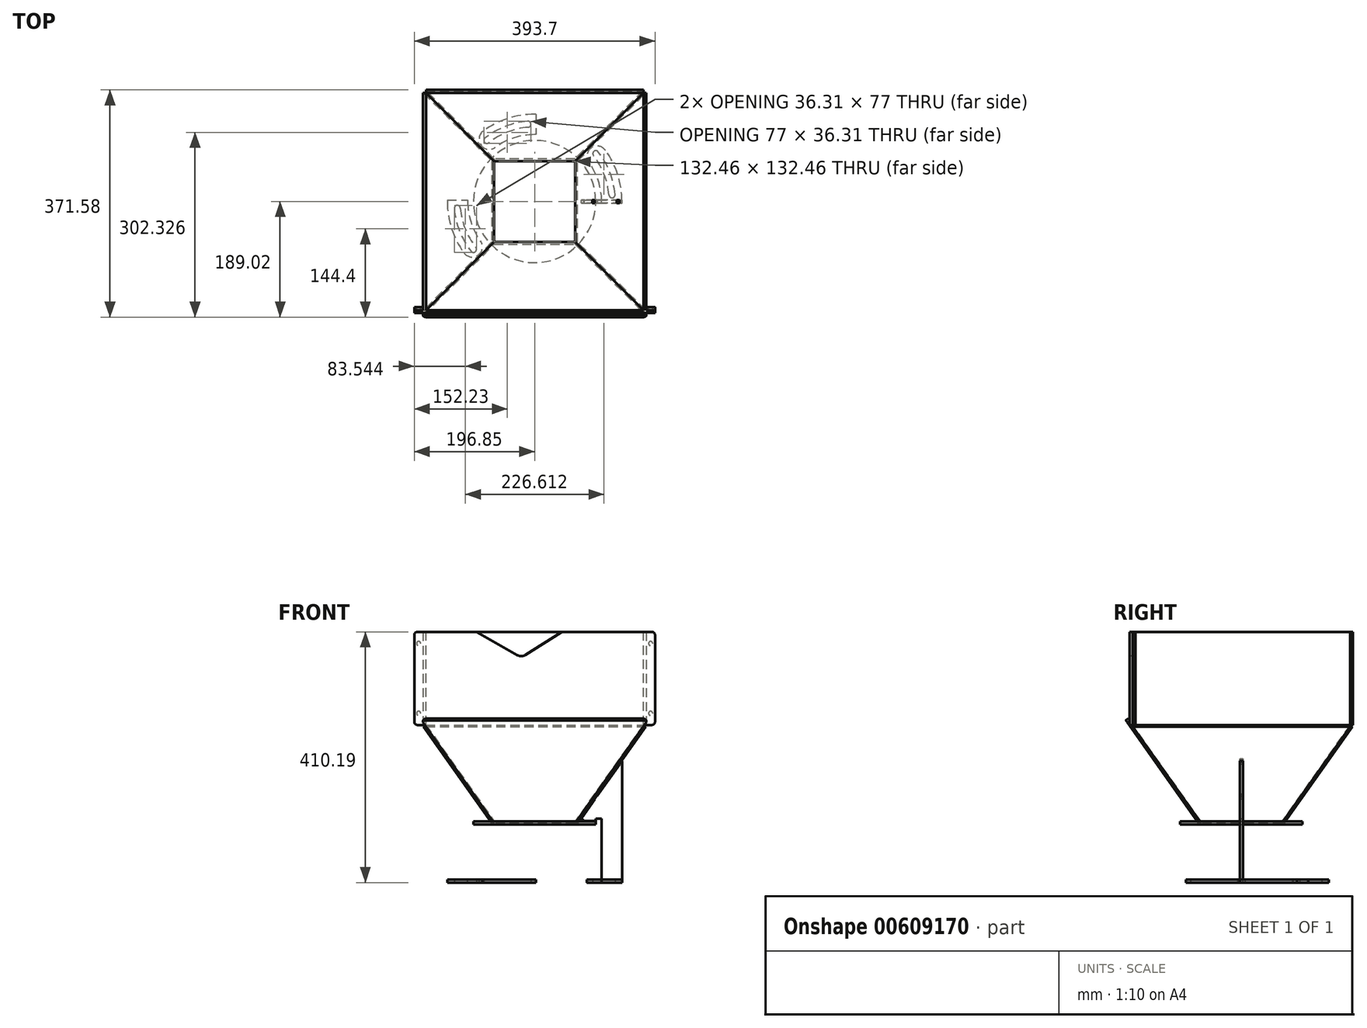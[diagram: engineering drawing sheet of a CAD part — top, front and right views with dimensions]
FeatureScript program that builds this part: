
annotation { "Feature Type Name" : "Feature", "Feature Type Description" : "" }
export const myFeature = defineFeature(function(context is Context, id is Id, definition is map)
    precondition{}
    {
        {
            var Q0;
            Q0=qCreatedBy(makeId("Top.planeOp"),FACE);
            var sketch = newSketch(context, id + "F0", { "sketchPlane" : qUnion([Q0])});
            skCircle(sketch, "E0", {"center": v(0, 0) * mm, "radius": 93.66 * mm});
            skLineSegment(sketch, "E1.bottom", {"start": v(66.23, 66.23) * mm, "end": v(-66.23, 66.23) * mm});
            skLineSegment(sketch, "E1.top", {"start": v(66.23, -66.23) * mm, "end": v(-66.23, -66.23) * mm});
            skLineSegment(sketch, "E1.left", {"start": v(66.23, 66.23) * mm, "end": v(66.23, -66.23) * mm});
            skLineSegment(sketch, "E1.right", {"start": v(-66.23, 66.23) * mm, "end": v(-66.23, -66.23) * mm});
            skCircle(sketch, "E2", {"center": v(0, 0) * mm, "radius": 100.01 * mm});
            skSolve(sketch);
        }
        {
            var Q0;
            Q0=qCreatedBy(makeId("Front.planeOp"),FACE);
            var sketch = newSketch(context, id + "F1", { "sketchPlane" : qUnion([Q0])});
            skLineSegment(sketch, "E3", {"start": v(66.23, 0) * mm, "end": v(177.8, 111.57) * mm});
            skLineSegment(sketch, "E4", {"start": v(66.23, 0) * mm, "end": v(0, 0) * mm, "construction": true});
            skLineSegment(sketch, "E5", {"start": v(0, 0) * mm, "end": v(0, 147.72) * mm, "construction": true});
            skSolve(sketch);
        }
        {
            var Q0;
            Q0=sQuery(id+"F1.wireOp",VERTEX,"E5.end");
            var Q1;
            Q1=sQuery(id+"F0.wireOp",VERTEX,"E0.center");
            var Q2;
            Q2=sQuery(id+"F0.wireOp",VERTEX,"E1.bottom.start");
            cPlane(context, id + "F2", {"entities" : qUnion([Q0, Q1, Q2]), "cplaneType" : CPlaneType.THREE_POINT, "offset" : 25.4 * mm, "width" : 152.4 * mm, "height" : 152.4 * mm});
        }
        {
            var Q0;
            Q0=qCreatedBy(id+"F2.planeOp",FACE);
            var sketch = newSketch(context, id + "F3", { "sketchPlane" : qUnion([Q0])});
            skLineSegment(sketch, "E6", {"start": v(0, 0) * mm, "end": v(-93.66, 0) * mm, "construction": true});
            skLineSegment(sketch, "E7", {"start": v(-93.66, 0) * mm, "end": v(-251.45, 157.78) * mm, "construction": true});
            skSolve(sketch);
        }
        {
            var Q0;
            Q0=sQuery(id+"F3.wireOp",VERTEX,"E7.end");
            var Q1;
            Q1=sQuery(id+"F1.wireOp",VERTEX,"E3.start");
            var Q2;
            Q2=sQuery(id+"F3.wireOp",VERTEX,"E7.start");
            cPlane(context, id + "F4", {"entities" : qUnion([Q0, Q1, Q2]), "cplaneType" : CPlaneType.THREE_POINT, "offset" : 25.4 * mm, "width" : 152.4 * mm, "height" : 152.4 * mm});
        }
        {
            var Q0;
            Q0=qCreatedBy(id+"F4.planeOp",FACE);
            var sketch = newSketch(context, id + "F5", { "sketchPlane" : qUnion([Q0])});
            skLineSegment(sketch, "E8", {"start": v(66.23, 38.24) * mm, "end": v(-66.23, 38.24) * mm});
            skLineSegment(sketch, "E9", {"start": v(-66.23, 38.24) * mm, "end": v(-177.8, 231.48) * mm});
            skLineSegment(sketch, "E10", {"start": v(-177.8, 231.48) * mm, "end": v(177.8, 231.48) * mm});
            skLineSegment(sketch, "E11", {"start": v(177.8, 231.48) * mm, "end": v(66.23, 38.24) * mm});
            skLineSegment(sketch, "E12", {"start": v(0, 38.24) * mm, "end": v(0, 231.48) * mm, "construction": true});
            skSolve(sketch);
        }
        {
            var Q0;
            Q0=makeQuery(id+"F5.imprint","IMPRINT",FACE,{"disambiguationData":[TD([[makeQuery(id+"F5.imprint","IMPRINT",EDGE,{"derivedFrom":sQuery(id+"F5.wireOp",EDGE,"E8")}),-1.0]])]});
            extrude(context, id + "F6", {"entities" : qUnion([Q0]), "oppositeDirection" : true, "depth" : 4.76 * mm, "offsetDistance" : 25.4 * mm});
        }
        {
            var Q0;
            Q0=qCreatedBy(makeId("Right.planeOp"),FACE);
            var Q1;
            Q1=makeQuery(id+"F6.opExtrude","CAP_VERTEX",VERTEX,{"disambiguationData":[OSD([sQuery(id+"F5.wireOp",EDGE,"E10"),sQuery(id+"F5.wireOp",EDGE,"E11")])],"isStart":true});
            cPlane(context, id + "F7", {"entities" : qUnion([Q0, Q1]), "cplaneType" : CPlaneType.PLANE_POINT, "offset" : 25.4 * mm, "width" : 152.4 * mm, "height" : 152.4 * mm});
        }
        {
            var Q0;
            Q0=qCreatedBy(id+"F7.planeOp",FACE);
            var sketch = newSketch(context, id + "F8", { "sketchPlane" : qUnion([Q0])});
            skLineSegment(sketch, "E13.bottom", {"start": v(-177.8, 157.78) * mm, "end": v(177.8, 157.78) * mm});
            skLineSegment(sketch, "E13.top", {"start": v(-177.8, 310.18) * mm, "end": v(177.8, 310.18) * mm});
            skLineSegment(sketch, "E13.left", {"start": v(-177.8, 157.78) * mm, "end": v(-177.8, 310.18) * mm});
            skLineSegment(sketch, "E13.right", {"start": v(177.8, 157.78) * mm, "end": v(177.8, 310.18) * mm});
            skSolve(sketch);
        }
        {
            var Q0;
            Q0=makeQuery(id+"F8.imprint","IMPRINT",FACE,{"disambiguationData":[TD([[makeQuery(id+"F8.imprint","IMPRINT",EDGE,{"derivedFrom":sQuery(id+"F8.wireOp",EDGE,"E13.bottom")}),1.0]])]});
            extrude(context, id + "F9", {"entities" : qUnion([Q0]), "depth" : 4.76 * mm, "offsetDistance" : 25.4 * mm});
        }
        {
            var Q0;
            Q0=makeQuery(id+"F6.opExtrude","SWEPT_BODY",BODY,{"disambiguationData":[OSD([sQuery(id+"F5.wireOp",EDGE,"E8"),sQuery(id+"F5.wireOp",EDGE,"E9"),sQuery(id+"F5.wireOp",EDGE,"E10"),sQuery(id+"F5.wireOp",EDGE,"E11")])]});
            var Q1;
            Q1=makeQuery(id+"F9.opExtrude","SWEPT_BODY",BODY,{"disambiguationData":[OSD([sQuery(id+"F8.wireOp",EDGE,"E13.bottom"),sQuery(id+"F8.wireOp",EDGE,"E13.top"),sQuery(id+"F8.wireOp",EDGE,"E13.left"),sQuery(id+"F8.wireOp",EDGE,"E13.right")])]});
            var Q2;
            Q2=sQuery(id+"F1.wireOp",EDGE,"E5");
            circularPattern(context, id + "F10", {"entities" : qUnion([Q0, Q1]), "axis" : qUnion([Q2]), "angle" : 360 * degree, "instanceCount" : 4, "equalSpace" : true});
        }
        {
            var Q0;
            Q0=makeQuery(id+"F0.imprint","IMPRINT",FACE,{"disambiguationData":[TD([[makeQuery(id+"F0.imprint","IMPRINT",EDGE,{"derivedFrom":sQuery(id+"F0.wireOp",EDGE,"E2")}),1.0]])]});
            var Q1;
            {var subQ0=sQuery(id+"F0.wireOp",EDGE,"E1.right");Q1=makeQuery(id+"F0.imprint","IMPRINT",FACE,{"disambiguationData":[TD([[makeQuery(id+"F0.imprint","IMPRINT",EDGE,{"derivedFrom":subQ0}),-1.0]])]});}
            var Q2;
            {var subQ0=sQuery(id+"F0.wireOp",EDGE,"E1.bottom");Q2=makeQuery(id+"F0.imprint","IMPRINT",FACE,{"disambiguationData":[TD([[makeQuery(id+"F0.imprint","IMPRINT",EDGE,{"derivedFrom":subQ0}),-1.0]])]});}
            var Q3;
            {var subQ0=sQuery(id+"F0.wireOp",EDGE,"E1.left");Q3=makeQuery(id+"F0.imprint","IMPRINT",FACE,{"disambiguationData":[TD([[makeQuery(id+"F0.imprint","IMPRINT",EDGE,{"derivedFrom":subQ0}),1.0]])]});}
            var Q4;
            {var subQ0=sQuery(id+"F0.wireOp",EDGE,"E1.top");Q4=makeQuery(id+"F0.imprint","IMPRINT",FACE,{"disambiguationData":[TD([[makeQuery(id+"F0.imprint","IMPRINT",EDGE,{"derivedFrom":subQ0}),1.0]])]});}
            extrude(context, id + "F11", {"entities" : qUnion([Q0, Q1, Q2, Q3, Q4]), "oppositeDirection" : true, "depth" : 4.76 * mm, "offsetDistance" : 25.4 * mm});
        }
        {
            var Q0;
            Q0=qCreatedBy(makeId("Front.planeOp"),FACE);
            var sketch = newSketch(context, id + "F12", { "sketchPlane" : qUnion([Q0])});
            skLineSegment(sketch, "E14", {"start": v(76.19, 4.46) * mm, "end": v(142.88, 98.77) * mm});
            skLineSegment(sketch, "E15", {"start": v(142.88, 98.77) * mm, "end": v(142.88, -95.25) * mm});
            skLineSegment(sketch, "E16", {"start": v(142.88, -95.25) * mm, "end": v(109.54, -95.25) * mm});
            skLineSegment(sketch, "E17", {"start": v(109.54, -95.25) * mm, "end": v(109.54, 4.76) * mm});
            skLineSegment(sketch, "E18", {"start": v(109.54, 4.76) * mm, "end": v(100.01, 4.76) * mm});
            skLineSegment(sketch, "E19", {"start": v(100.01, 4.76) * mm, "end": v(100.01, 0.8) * mm});
            skLineSegment(sketch, "E20", {"start": v(100.01, 0.8) * mm, "end": v(81.37, 0.8) * mm});
            skLineSegment(sketch, "E21", {"start": v(81.37, 0.8) * mm, "end": v(76.19, 4.46) * mm});
            skLineSegment(sketch, "E22", {"start": v(100.01, 0.8) * mm, "end": v(100.01, 0) * mm, "construction": true});
            skSolve(sketch);
        }
        {
            var Q0;
            Q0 = qSketchRegion(id + "F12", true);
            extrude(context, id + "F13", {"entities" : qUnion([Q0]), "endBound" : BoundingType.SYMMETRIC, "depth" : 4.76 * mm, "offsetDistance" : 25.4 * mm});
        }
        {
            var Q0;
            Q0=makeQuery(id+"F13.opExtrude","SWEPT_FACE",FACE,{"disambiguationData":[OSD([sQuery(id+"F12.wireOp",EDGE,"E16")])]});
            var sketch = newSketch(context, id + "F14", { "sketchPlane" : qUnion([Q0])});
            skArc(sketch, "E23", {"start": v(109.54, 0) * mm, "mid": v(104.18, -33.85) * mm, "end": v(88.62, -64.38) * mm});
            skArc(sketch, "E24", {"start": v(142.88, 0) * mm, "mid": v(135.88, -44.15) * mm, "end": v(115.59, -83.98) * mm});
            skArc(sketch, "E25", {"start": v(88.62, -64.38) * mm, "mid": v(92.3, -87.67) * mm, "end": v(115.59, -83.98) * mm});
            skLineSegment(sketch, "E26", {"start": v(0, 0) * mm, "end": v(102.1, -74.18) * mm, "construction": true});
            skLineSegment(sketch, "E27", {"start": v(109.54, 0) * mm, "end": v(109.54, 2.38) * mm});
            skLineSegment(sketch, "E28", {"start": v(109.54, 2.38) * mm, "end": v(142.88, 2.38) * mm});
            skLineSegment(sketch, "E29", {"start": v(142.88, 2.38) * mm, "end": v(142.88, 0) * mm});
            skSolve(sketch);
        }
        {
            var Q0;
            Q0 = qSketchRegion(id + "F14", true);
            extrude(context, id + "F15", {"entities" : qUnion([Q0]), "depth" : 4.76 * mm, "offsetDistance" : 25.4 * mm});
        }
        {
            var Q0;
            Q0=makeQuery(id+"F15.opExtrude","CAP_FACE",FACE,{"disambiguationData":[OSD([sQuery(id+"F14.wireOp",EDGE,"E23"),sQuery(id+"F14.wireOp",EDGE,"E24"),sQuery(id+"F14.wireOp",EDGE,"E25"),sQuery(id+"F14.wireOp",EDGE,"E27"),sQuery(id+"F14.wireOp",EDGE,"E28"),sQuery(id+"F14.wireOp",EDGE,"E29")])],"isStart":false});
            var sketch = newSketch(context, id + "F16", { "sketchPlane" : qUnion([Q0])});
            skArc(sketch, "E30", {"start": v(126.52, -11.07) * mm, "mid": v(118.16, -46.55) * mm, "end": v(100.08, -78.19) * mm, "construction": true});
            skArc(sketch, "E31.0.startCap", {"start": v(121.57, -10.64) * mm, "mid": v(126.95, -6.12) * mm, "end": v(131.46, -11.5) * mm});
            skArc(sketch, "E31.0.endCap", {"start": v(104, -81.25) * mm, "mid": v(97.02, -82.1) * mm, "end": v(96.16, -75.13) * mm});
            skArc(sketch, "E31.0.left", {"start": v(131.46, -11.5) * mm, "mid": v(122.78, -48.37) * mm, "end": v(104, -81.25) * mm});
            skArc(sketch, "E31.0.right", {"start": v(121.57, -10.64) * mm, "mid": v(113.54, -44.73) * mm, "end": v(96.16, -75.13) * mm});
            skLineSegment(sketch, "E32", {"start": v(126.52, -11.07) * mm, "end": v(0, 0) * mm, "construction": true});
            skLineSegment(sketch, "E33", {"start": v(100.08, -78.19) * mm, "end": v(0, 0) * mm, "construction": true});
            skSolve(sketch);
        }
        {
            var Q0;
            Q0 = qSketchRegion(id + "F16", true);
            var Q1;
            Q1=makeQuery(id+"F15.opExtrude","CAP_FACE",FACE,{"disambiguationData":[OSD([sQuery(id+"F14.wireOp",EDGE,"E23"),sQuery(id+"F14.wireOp",EDGE,"E24"),sQuery(id+"F14.wireOp",EDGE,"E25"),sQuery(id+"F14.wireOp",EDGE,"E27"),sQuery(id+"F14.wireOp",EDGE,"E28"),sQuery(id+"F14.wireOp",EDGE,"E29")])],"isStart":true});
            extrude(context, id + "F17", {"entities" : qUnion([Q0]), "operationType" : NewBodyOperationType.REMOVE, "endBound" : BoundingType.UP_TO_SURFACE, "oppositeDirection" : true, "depth" : 25.4 * mm, "endBoundEntityFace" : qUnion([Q1]), "offsetDistance" : 25.4 * mm});
        }
        {
            var Q0;
            Q0=makeQuery(id+"F13.opExtrude","SWEPT_FACE",FACE,{"disambiguationData":[OSD([sQuery(id+"F12.wireOp",EDGE,"E14")])]});
            var sketch = newSketch(context, id + "F18", { "sketchPlane" : qUnion([Q0])});
            skLineSegment(sketch, "E34.bottom", {"start": v(-2.38, 163.13) * mm, "end": v(2.38, 163.13) * mm});
            skLineSegment(sketch, "E34.top", {"start": v(-2.38, 156.78) * mm, "end": v(2.38, 156.78) * mm});
            skLineSegment(sketch, "E34.left", {"start": v(-2.38, 163.13) * mm, "end": v(-2.38, 156.78) * mm});
            skLineSegment(sketch, "E34.right", {"start": v(2.38, 163.13) * mm, "end": v(2.38, 156.78) * mm});
            skLineSegment(sketch, "E35.bottom", {"start": v(-2.38, 93.28) * mm, "end": v(2.38, 93.28) * mm});
            skLineSegment(sketch, "E35.top", {"start": v(-2.38, 86.93) * mm, "end": v(2.38, 86.93) * mm});
            skLineSegment(sketch, "E35.left", {"start": v(-2.38, 93.28) * mm, "end": v(-2.38, 86.93) * mm});
            skLineSegment(sketch, "E35.right", {"start": v(2.38, 93.28) * mm, "end": v(2.38, 86.93) * mm});
            skSolve(sketch);
        }
        {
            var Q0;
            Q0 = qSketchRegion(id + "F18", true);
            extrude(context, id + "F19", {"entities" : qUnion([Q0]), "operationType" : NewBodyOperationType.ADD, "depth" : 4.76 * mm, "offsetDistance" : 25.4 * mm});
        }
        {
            var Q0;
            Q0=makeQuery(id+"F6.opExtrude","CAP_FACE",FACE,{"disambiguationData":[OSD([sQuery(id+"F5.wireOp",EDGE,"E8"),sQuery(id+"F5.wireOp",EDGE,"E9"),sQuery(id+"F5.wireOp",EDGE,"E10"),sQuery(id+"F5.wireOp",EDGE,"E11")])],"isStart":false});
            var sketch = newSketch(context, id + "F20", { "sketchPlane" : qUnion([Q0])});
            skLineSegment(sketch, "E36.0", {"start": v(-2.64, 163.39) * mm, "end": v(2.64, 163.39) * mm});
            skLineSegment(sketch, "E37", {"start": v(-2.64, 163.39) * mm, "end": v(-2.64, 156.53) * mm});
            skLineSegment(sketch, "E38", {"start": v(-2.64, 156.53) * mm, "end": v(2.64, 156.53) * mm});
            skLineSegment(sketch, "E39", {"start": v(2.64, 156.53) * mm, "end": v(2.64, 163.39) * mm});
            skLineSegment(sketch, "E40.0", {"start": v(2.64, 93.54) * mm, "end": v(-2.64, 93.54) * mm});
            skLineSegment(sketch, "E41", {"start": v(-2.64, 93.54) * mm, "end": v(-2.64, 86.68) * mm});
            skLineSegment(sketch, "E42", {"start": v(-2.64, 86.68) * mm, "end": v(2.64, 86.68) * mm});
            skLineSegment(sketch, "E43", {"start": v(2.64, 86.68) * mm, "end": v(2.64, 93.54) * mm});
            skSolve(sketch);
        }
        {
            var Q0;
            Q0 = qSketchRegion(id + "F20", true);
            extrude(context, id + "F21", {"entities" : qUnion([Q0]), "operationType" : NewBodyOperationType.REMOVE, "oppositeDirection" : true, "depth" : 6.35 * mm, "offsetDistance" : 25.4 * mm});
        }
        {
            var Q0;
            Q0=makeQuery(id+"F13.opExtrude","SWEPT_BODY",BODY,{"disambiguationData":[OSD([sQuery(id+"F12.wireOp",EDGE,"E14"),sQuery(id+"F12.wireOp",EDGE,"E15"),sQuery(id+"F12.wireOp",EDGE,"E16"),sQuery(id+"F12.wireOp",EDGE,"E17"),sQuery(id+"F12.wireOp",EDGE,"E18"),sQuery(id+"F12.wireOp",EDGE,"E19"),sQuery(id+"F12.wireOp",EDGE,"E20"),sQuery(id+"F12.wireOp",EDGE,"E21")])]});
            var Q1;
            Q1=makeQuery(id+"F15.opExtrude","SWEPT_BODY",BODY,{"disambiguationData":[OSD([sQuery(id+"F14.wireOp",EDGE,"E23"),sQuery(id+"F14.wireOp",EDGE,"E24"),sQuery(id+"F14.wireOp",EDGE,"E25"),sQuery(id+"F14.wireOp",EDGE,"E27"),sQuery(id+"F14.wireOp",EDGE,"E28"),sQuery(id+"F14.wireOp",EDGE,"E29")])]});
            var Q2;
            Q2=makeQuery(id+"F11.opExtrude","CAP_EDGE",EDGE,{"disambiguationData":[OSD([sQuery(id+"F0.wireOp",EDGE,"E2")])],"isStart":false});
            circularPattern(context, id + "F22", {"entities" : qUnion([Q0, Q1]), "axis" : qUnion([Q2]), "angle" : 180 * degree, "instanceCount" : 3, "equalSpace" : true});
        }
        {
            var Q0;
            Q0=makeQuery(id+"F10.opPattern","COPY",FACE,{"derivedFrom":makeQuery(id+"F6.opExtrude","CAP_FACE",FACE,{"disambiguationData":[OSD([sQuery(id+"F5.wireOp",EDGE,"E8"),sQuery(id+"F5.wireOp",EDGE,"E9"),sQuery(id+"F5.wireOp",EDGE,"E10"),sQuery(id+"F5.wireOp",EDGE,"E11")])],"isStart":false}),"instanceName":"3"});
            var sketch = newSketch(context, id + "F23", { "sketchPlane" : qUnion([Q0])});
            skLineSegment(sketch, "E44.bottom", {"start": v(-177.8, 231.48) * mm, "end": v(177.8, 231.48) * mm});
            skLineSegment(sketch, "E44.top", {"start": v(-182.56, 244.18) * mm, "end": v(182.56, 244.18) * mm});
            skLineSegment(sketch, "E45", {"start": v(-177.8, 231.48) * mm, "end": v(-182.56, 239.73) * mm});
            skLineSegment(sketch, "E46", {"start": v(-182.56, 239.73) * mm, "end": v(-182.56, 244.18) * mm});
            skLineSegment(sketch, "E47", {"start": v(177.8, 231.48) * mm, "end": v(182.56, 239.73) * mm});
            skLineSegment(sketch, "E48", {"start": v(182.56, 239.73) * mm, "end": v(182.56, 244.18) * mm});
            skSolve(sketch);
        }
        {
            var Q0;
            Q0 = qSketchRegion(id + "F23", true);
            var Q1;
            Q1=makeQuery(id+"F10.opPattern","COPY",FACE,{"derivedFrom":makeQuery(id+"F6.opExtrude","CAP_FACE",FACE,{"disambiguationData":[OSD([sQuery(id+"F5.wireOp",EDGE,"E8"),sQuery(id+"F5.wireOp",EDGE,"E9"),sQuery(id+"F5.wireOp",EDGE,"E10"),sQuery(id+"F5.wireOp",EDGE,"E11")])],"isStart":true}),"instanceName":"3"});
            extrude(context, id + "F24", {"entities" : qUnion([Q0]), "operationType" : NewBodyOperationType.ADD, "endBound" : BoundingType.UP_TO_SURFACE, "oppositeDirection" : true, "depth" : 25.4 * mm, "endBoundEntityFace" : qUnion([Q1]), "offsetDistance" : 25.4 * mm});
        }
        {
            var Q0;
            Q0=makeQuery(id+"F10.opPattern","COPY",FACE,{"derivedFrom":makeQuery(id+"F9.opExtrude","CAP_FACE",FACE,{"disambiguationData":[OSD([sQuery(id+"F8.wireOp",EDGE,"E13.bottom"),sQuery(id+"F8.wireOp",EDGE,"E13.top"),sQuery(id+"F8.wireOp",EDGE,"E13.left"),sQuery(id+"F8.wireOp",EDGE,"E13.right")])],"isStart":false}),"instanceName":"3"});
            var sketch = newSketch(context, id + "F25", { "sketchPlane" : qUnion([Q0])});
            skLineSegment(sketch, "E49.bottom", {"start": v(177.8, 310.18) * mm, "end": v(196.85, 310.18) * mm});
            skLineSegment(sketch, "E49.top", {"start": v(177.8, 157.78) * mm, "end": v(196.85, 157.78) * mm});
            skLineSegment(sketch, "E49.left", {"start": v(177.8, 310.18) * mm, "end": v(177.8, 157.78) * mm});
            skLineSegment(sketch, "E49.right", {"start": v(196.85, 310.18) * mm, "end": v(196.85, 157.78) * mm});
            skLineSegment(sketch, "E50.bottom", {"start": v(-177.8, 310.18) * mm, "end": v(-196.85, 310.18) * mm});
            skLineSegment(sketch, "E50.top", {"start": v(-177.8, 157.78) * mm, "end": v(-196.85, 157.78) * mm});
            skLineSegment(sketch, "E50.left", {"start": v(-177.8, 310.18) * mm, "end": v(-177.8, 157.78) * mm});
            skLineSegment(sketch, "E50.right", {"start": v(-196.85, 310.18) * mm, "end": v(-196.85, 157.78) * mm});
            skSolve(sketch);
        }
        {
            var Q0;
            Q0 = qSketchRegion(id + "F25", true);
            var Q1;
            Q1=makeQuery(id+"F10.opPattern","COPY",FACE,{"derivedFrom":makeQuery(id+"F9.opExtrude","CAP_FACE",FACE,{"disambiguationData":[OSD([sQuery(id+"F8.wireOp",EDGE,"E13.bottom"),sQuery(id+"F8.wireOp",EDGE,"E13.top"),sQuery(id+"F8.wireOp",EDGE,"E13.left"),sQuery(id+"F8.wireOp",EDGE,"E13.right")])],"isStart":true}),"instanceName":"3"});
            extrude(context, id + "F26", {"entities" : qUnion([Q0]), "operationType" : NewBodyOperationType.ADD, "endBound" : BoundingType.UP_TO_SURFACE, "oppositeDirection" : true, "depth" : 25.4 * mm, "endBoundEntityFace" : qUnion([Q1]), "offsetDistance" : 25.4 * mm});
        }
        {
            var Q0;
            {var subQ0=sQuery(id+"F8.wireOp",EDGE,"E13.right");var subQ1=sQuery(id+"F8.wireOp",EDGE,"E13.left");var subQ2=sQuery(id+"F8.wireOp",EDGE,"E13.top");var subQ3=sQuery(id+"F8.wireOp",EDGE,"E13.bottom");Q0=makeQuery(id+"F26.boolean.opBoolean","MERGE",FACE,{"derivedFrom":[makeQuery(id+"F10.opPattern","COPY",FACE,{"derivedFrom":makeQuery(id+"F9.opExtrude","CAP_FACE",FACE,{"disambiguationData":[OSD([subQ3,subQ2,subQ1,subQ0])],"isStart":true}),"instanceName":"3"}),makeQuery(id+"F26.opExtrude","CAP_FACE",FACE,{"disambiguationData":[OSD([subQ3,subQ2,subQ1,subQ0]),OD(0.0)],"isStart":false}),makeQuery(id+"F26.opExtrude","CAP_FACE",FACE,{"disambiguationData":[OSD([subQ3,subQ2,subQ1,subQ0]),OD(1.0)],"isStart":false})]});}
            var sketch = newSketch(context, id + "F27", { "sketchPlane" : qUnion([Q0])});
            skLineSegment(sketch, "E51.bottom", {"start": v(182.56, 310.18) * mm, "end": v(196.85, 310.18) * mm});
            skLineSegment(sketch, "E51.top", {"start": v(182.56, 157.78) * mm, "end": v(196.85, 157.78) * mm});
            skLineSegment(sketch, "E51.left", {"start": v(182.56, 310.18) * mm, "end": v(182.56, 157.78) * mm});
            skLineSegment(sketch, "E51.right", {"start": v(196.85, 310.18) * mm, "end": v(196.85, 157.78) * mm});
            skSolve(sketch);
        }
        {
            var Q0;
            Q0 = qSketchRegion(id + "F27", true);
            extrude(context, id + "F28", {"entities" : qUnion([Q0]), "depth" : 4.76 * mm, "offsetDistance" : 25.4 * mm});
        }
        {
            var Q0;
            Q0=makeQuery(id+"F28.opExtrude","CAP_FACE",FACE,{"disambiguationData":[OSD([sQuery(id+"F27.wireOp",EDGE,"E51.bottom"),sQuery(id+"F27.wireOp",EDGE,"E51.top"),sQuery(id+"F27.wireOp",EDGE,"E51.left"),sQuery(id+"F27.wireOp",EDGE,"E51.right")])],"isStart":false});
            var sketch = newSketch(context, id + "F29", { "sketchPlane" : qUnion([Q0])});
            skLineSegment(sketch, "E52", {"start": v(189.7, 291.13) * mm, "end": v(189.7, 176.83) * mm, "construction": true});
            skLineSegment(sketch, "E53", {"start": v(182.56, 233.98) * mm, "end": v(196.85, 233.98) * mm, "construction": true});
            skPoint(sketch, "E54", {"position": v(189.7, 233.98) * mm});
            skSolve(sketch);
        }
        {
            var Q0;
            Q0=makeQuery(id+"F28.opExtrude","SWEPT_EDGE",EDGE,{"disambiguationData":[OSD([sQuery(id+"F27.wireOp",EDGE,"E51.bottom"),sQuery(id+"F27.wireOp",EDGE,"E51.right")])]});
            var Q1;
            Q1=makeQuery(id+"F26.opExtrude","SWEPT_EDGE",EDGE,{"disambiguationData":[OSD([sQuery(id+"F25.wireOp",EDGE,"E50.bottom"),sQuery(id+"F25.wireOp",EDGE,"E50.right")])]});
            var Q2;
            Q2=makeQuery(id+"F28.opExtrude","SWEPT_EDGE",EDGE,{"disambiguationData":[OSD([sQuery(id+"F27.wireOp",EDGE,"E51.top"),sQuery(id+"F27.wireOp",EDGE,"E51.right")])]});
            var Q3;
            Q3=makeQuery(id+"F26.opExtrude","SWEPT_EDGE",EDGE,{"disambiguationData":[OSD([sQuery(id+"F25.wireOp",EDGE,"E50.top"),sQuery(id+"F25.wireOp",EDGE,"E50.right")])]});
            var Q4;
            Q4=makeQuery(id+"F26.opExtrude","SWEPT_EDGE",EDGE,{"disambiguationData":[OSD([sQuery(id+"F25.wireOp",EDGE,"E49.bottom"),sQuery(id+"F25.wireOp",EDGE,"E49.right")])]});
            var Q5;
            Q5=makeQuery(id+"F26.opExtrude","SWEPT_EDGE",EDGE,{"disambiguationData":[OSD([sQuery(id+"F25.wireOp",EDGE,"E49.top"),sQuery(id+"F25.wireOp",EDGE,"E49.right")])]});
            var Q6;
            Q6=makeQuery(id+"F24.opExtrude","SWEPT_EDGE",EDGE,{"disambiguationData":[OSD([sQuery(id+"F23.wireOp",EDGE,"E44.top"),sQuery(id+"F23.wireOp",EDGE,"E48")])]});
            var Q7;
            Q7=makeQuery(id+"F24.opExtrude","SWEPT_EDGE",EDGE,{"disambiguationData":[OSD([sQuery(id+"F23.wireOp",EDGE,"E44.top"),sQuery(id+"F23.wireOp",EDGE,"E46")])]});
            fillet(context, id + "F30", {"entities" : qUnion([Q0, Q1, Q2, Q3, Q4, Q5, Q6, Q7]), "radius" : 5.08 * mm, "tangentPropagation" : true, "allowEdgeOverflow" : false});
        }
        {
            var Q0;
            Q0=sQuery(id+"F29.wireOp",VERTEX,"E52.start");
            var Q1;
            Q1=sQuery(id+"F29.wireOp",VERTEX,"E52.end");
            var Q2;
            Q2=makeQuery(id+"F10.opPattern","COPY",BODY,{"derivedFrom":makeQuery(id+"F9.opExtrude","SWEPT_BODY",BODY,{"disambiguationData":[OSD([sQuery(id+"F8.wireOp",EDGE,"E13.bottom"),sQuery(id+"F8.wireOp",EDGE,"E13.top"),sQuery(id+"F8.wireOp",EDGE,"E13.left"),sQuery(id+"F8.wireOp",EDGE,"E13.right")])]}),"instanceName":"3"});
            var Q3;
            Q3=makeQuery(id+"F28.opExtrude","SWEPT_BODY",BODY,{"disambiguationData":[OSD([sQuery(id+"F27.wireOp",EDGE,"E51.bottom"),sQuery(id+"F27.wireOp",EDGE,"E51.top"),sQuery(id+"F27.wireOp",EDGE,"E51.left"),sQuery(id+"F27.wireOp",EDGE,"E51.right")])]});
            hole(context, id + "F31", {"style" : HoleStyle.SIMPLE, "endStyle" : HoleEndStyle.THROUGH, "standardTappedOrClearance" : lookupTablePath({ "standard" : "ANSI", "fit" : "Normal (ASME)", "size" : "1/4", "type" : "Clearance" }), "standardBlindInLast" : lookupTablePath({ "fit" : "Free", "standard" : "ANSI", "size" : "1/4", "type" : "Clearance" }), "holeDiameter" : 6.76 * mm, "majorDiameter" : 6.35 * mm, "isTappedThrough" : true, "tappedDepth" : 12.7 * mm, "tapClearance" : 3, "locations" : qUnion([Q0, Q1]), "scope" : qUnion([Q2, Q3])});
        }
        {
            var Q0;
            Q0=makeQuery(id+"F28.opExtrude","SWEPT_BODY",BODY,{"disambiguationData":[OSD([sQuery(id+"F27.wireOp",EDGE,"E51.bottom"),sQuery(id+"F27.wireOp",EDGE,"E51.top"),sQuery(id+"F27.wireOp",EDGE,"E51.left"),sQuery(id+"F27.wireOp",EDGE,"E51.right")])]});
            var Q1;
            Q1=qCreatedBy(makeId("Right.planeOp"),FACE);
            mirror(context, id + "F32", {"entities" : qUnion([Q0]), "mirrorPlane" : qUnion([Q1])});
        }
        {
            var Q0;
            Q0=makeQuery(id+"F26.boolean.opBoolean","MERGE",FACE,{"derivedFrom":[makeQuery(id+"F10.opPattern","COPY",FACE,{"derivedFrom":makeQuery(id+"F9.opExtrude","CAP_FACE",FACE,{"disambiguationData":[OSD([sQuery(id+"F8.wireOp",EDGE,"E13.bottom"),sQuery(id+"F8.wireOp",EDGE,"E13.top"),sQuery(id+"F8.wireOp",EDGE,"E13.left"),sQuery(id+"F8.wireOp",EDGE,"E13.right")])],"isStart":false}),"instanceName":"3"}),makeQuery(id+"F26.opExtrude","CAP_FACE",FACE,{"disambiguationData":[OSD([sQuery(id+"F25.wireOp",EDGE,"E49.bottom"),sQuery(id+"F25.wireOp",EDGE,"E49.top"),sQuery(id+"F25.wireOp",EDGE,"E49.left"),sQuery(id+"F25.wireOp",EDGE,"E49.right")])],"isStart":true}),makeQuery(id+"F26.opExtrude","CAP_FACE",FACE,{"disambiguationData":[OSD([sQuery(id+"F25.wireOp",EDGE,"E50.bottom"),sQuery(id+"F25.wireOp",EDGE,"E50.top"),sQuery(id+"F25.wireOp",EDGE,"E50.left"),sQuery(id+"F25.wireOp",EDGE,"E50.right")])],"isStart":true})]});
            var sketch = newSketch(context, id + "F33", { "sketchPlane" : qUnion([Q0])});
            skPoint(sketch, "E55", {"position": v(-21.84, 283.06) * mm});
            skLineSegment(sketch, "E56", {"start": v(-95.25, 310.18) * mm, "end": v(-28.12, 272.02) * mm});
            skArc(sketch, "E57", {"start": v(-28.12, 272.02) * mm, "mid": v(-21.53, 270.36) * mm, "end": v(-15.03, 272.34) * mm});
            skLineSegment(sketch, "E58", {"start": v(-15.03, 272.34) * mm, "end": v(44.45, 310.18) * mm});
            skLineSegment(sketch, "E59", {"start": v(-95.25, 310.18) * mm, "end": v(44.45, 310.18) * mm});
            skSolve(sketch);
        }
        {
            var Q0;
            Q0=makeQuery(id+"F33.imprint","IMPRINT",FACE,{"disambiguationData":[TD([[makeQuery(id+"F33.imprint","IMPRINT",EDGE,{"derivedFrom":sQuery(id+"F33.wireOp",EDGE,"E56")}),1.0]])]});
            extrude(context, id + "F34", {"entities" : qUnion([Q0]), "operationType" : NewBodyOperationType.REMOVE, "oppositeDirection" : true, "depth" : 25.4 * mm, "offsetDistance" : 25.4 * mm});
        }
        {
            var Q0;
            Q0=makeQuery(id+"F34.boolean.opBoolean","COPY",EDGE,{"derivedFrom":makeQuery(id+"F34.opExtrude","SWEPT_EDGE",EDGE,{"disambiguationData":[OSD([sQuery(id+"F8.wireOp",EDGE,"E13.top"),sQuery(id+"F25.wireOp",EDGE,"E49.bottom"),sQuery(id+"F25.wireOp",EDGE,"E50.bottom"),sQuery(id+"F33.wireOp",EDGE,"E56"),sQuery(id+"F33.wireOp",EDGE,"E59")])]})});
            var Q1;
            Q1=makeQuery(id+"F34.boolean.opBoolean","COPY",EDGE,{"derivedFrom":makeQuery(id+"F34.opExtrude","SWEPT_EDGE",EDGE,{"disambiguationData":[OSD([sQuery(id+"F8.wireOp",EDGE,"E13.top"),sQuery(id+"F25.wireOp",EDGE,"E49.bottom"),sQuery(id+"F25.wireOp",EDGE,"E50.bottom"),sQuery(id+"F33.wireOp",EDGE,"E58"),sQuery(id+"F33.wireOp",EDGE,"E59")])]})});
            fillet(context, id + "F35", {"entities" : qUnion([Q0, Q1]), "radius" : 5.08 * mm, "tangentPropagation" : true, "allowEdgeOverflow" : false});
        }
    });
